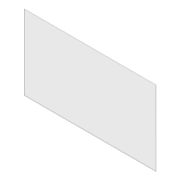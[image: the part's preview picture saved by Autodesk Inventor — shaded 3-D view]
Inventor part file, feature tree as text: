
AUTODESK INVENTOR PART (.ipt)
format: ipt  version: unknown  size: 160,768 bytes
history: native  units: in
note: dims shown in document units (in); Inventor stores cm internally (conversion verified against a paired STEP export)
features: extrude x1, sketch x1
ambient origin geometry x8: Origin, YZ Plane, XZ Plane, XY Plane, X Axis, Y Axis, Z Axis, Center Point
bodies: Solid1 (feature_tree)
feature tree (2):
  extrude  "Extrusion1"  Depth=28.5in
  sketch  "Sketch1"  dims[d0=50.0in d1=28.5in d7=0.25in d8=0.0in]
